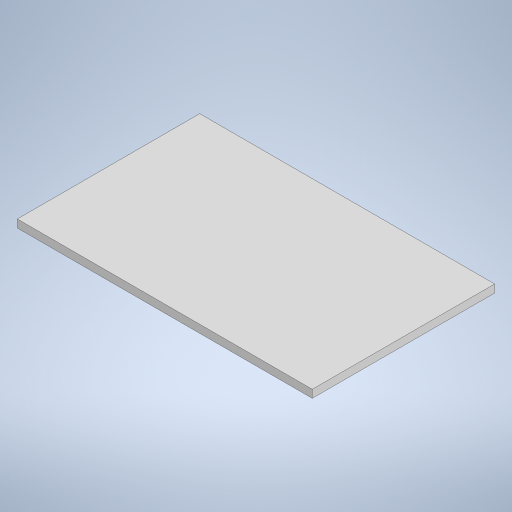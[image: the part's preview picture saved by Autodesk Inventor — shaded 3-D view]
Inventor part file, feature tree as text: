
AUTODESK INVENTOR PART (.ipt)
format: ipt  version: 2023 (Build 270158000, 158)  size: 202,752 bytes
history: native  units: mm
features: other x1, extrude x1, sketch x1
ambient origin geometry x8: Origin, YZ Plane, XZ Plane, XY Plane, X Axis, Y Axis, Z Axis, Center Point
bodies: Body1 (feature_tree)
feature tree (3):
  other  "ソリッド1"
  extrude  "押し出し1"  Depth=60.0mm
  sketch  "スケッチ1"
